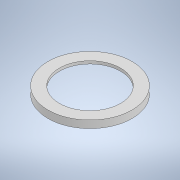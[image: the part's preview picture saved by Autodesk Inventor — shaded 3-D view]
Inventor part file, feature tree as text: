
AUTODESK INVENTOR PART (.ipt)
format: ipt  version: 2022 (Build 260153000, 153)  size: 114,688 bytes
history: native  units: mm
features: extrude x2, sketch x2
ambient origin geometry x8: Origin, YZ Plane, XZ Plane, XY Plane, X Axis, Y Axis, Z Axis, Center Point
bodies: Solid1 (feature_tree)
feature tree (4):
  extrude  "Extrusion1"  Depth=3.8mm
  extrude  "Extrusion2"  Depth=3.0mm
  sketch  "Sketch1"  dims[d1=83.0mm d2=3.8mm]
  sketch  "Sketch2"  dims[d3=5.0mm d4=0.0mm d5=8.5mm d6=3.0mm d7=0.0mm]
